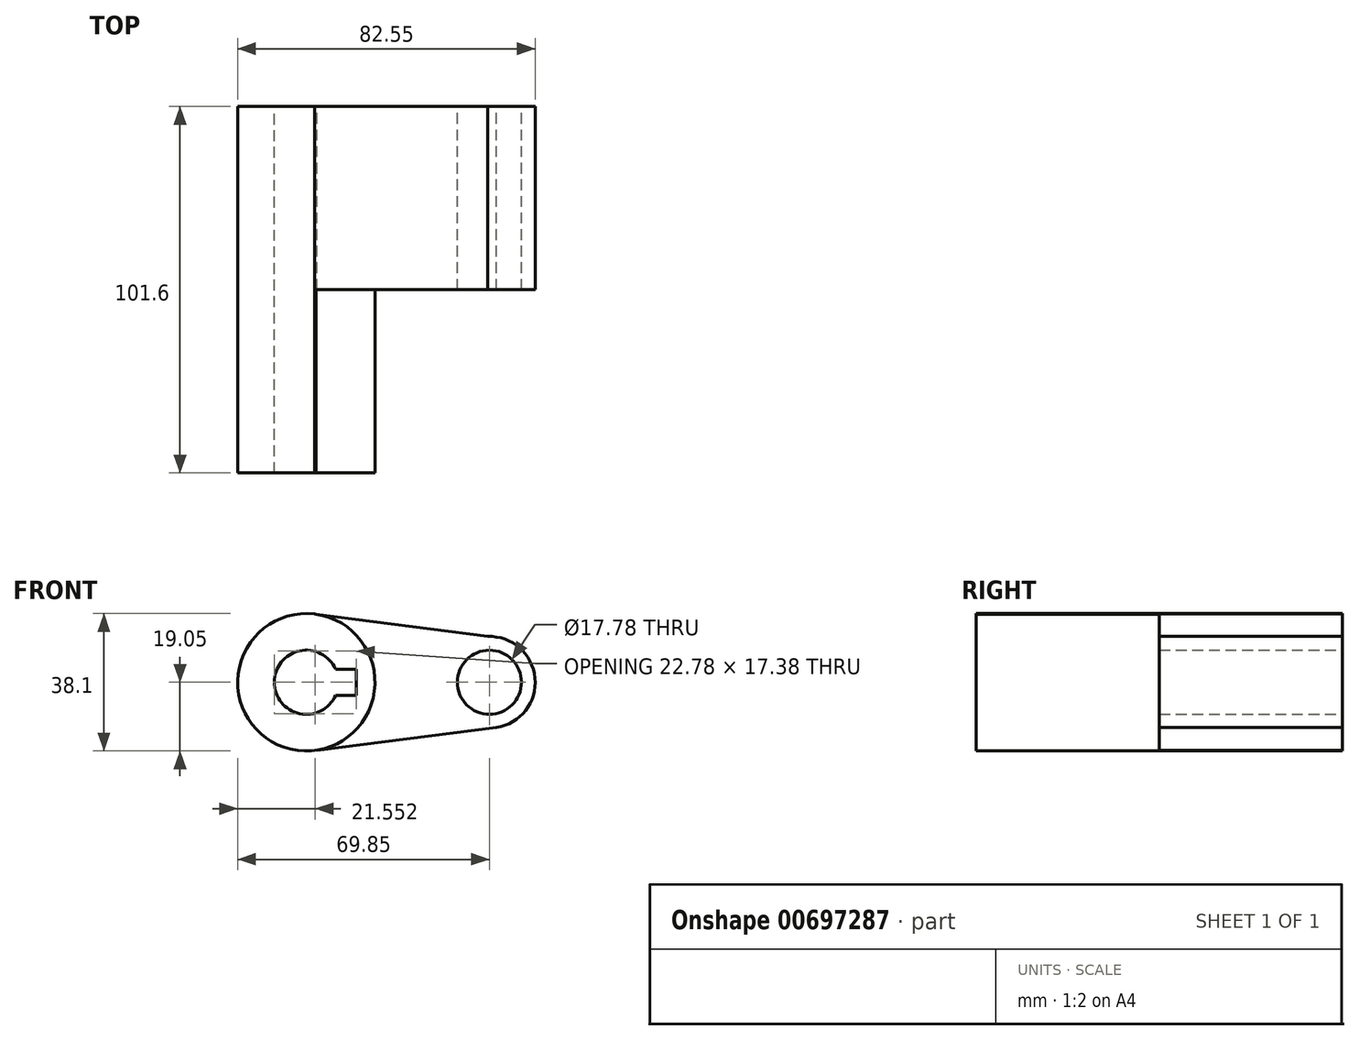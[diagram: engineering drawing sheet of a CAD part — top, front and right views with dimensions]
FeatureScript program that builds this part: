
annotation { "Feature Type Name" : "Feature", "Feature Type Description" : "" }
export const myFeature = defineFeature(function(context is Context, id is Id, definition is map)
    precondition{}
    {
        {
            var Q0;
            Q0=qCreatedBy(makeId("Front.planeOp"),FACE);
            var sketch = newSketch(context, id + "F0", { "sketchPlane" : qUnion([Q0])});
            skCircle(sketch, "E0", {"center": v(0, 0) * mm, "radius": 19.05 * mm});
            skCircle(sketch, "E1", {"center": v(50.8, 0) * mm, "radius": 12.7 * mm});
            skLineSegment(sketch, "E2", {"start": v(2.25, 18.92) * mm, "end": v(50.31, 12.7) * mm});
            skLineSegment(sketch, "E3", {"start": v(2.95, -18.82) * mm, "end": v(52.74, -12.55) * mm});
            skCircle(sketch, "E4", {"center": v(0, 0) * mm, "radius": 8.9 * mm});
            skCircle(sketch, "E5", {"center": v(50.8, 0) * mm, "radius": 8.9 * mm});
            skLineSegment(sketch, "E6.bottom", {"start": v(13.9, -3.65) * mm, "end": v(-13.9, -3.65) * mm});
            skLineSegment(sketch, "E6.top", {"start": v(13.9, 3.65) * mm, "end": v(-13.9, 3.65) * mm});
            skLineSegment(sketch, "E6.left", {"start": v(13.9, -3.65) * mm, "end": v(13.9, 3.65) * mm});
            skLineSegment(sketch, "E6.right", {"start": v(-13.9, -3.65) * mm, "end": v(-13.9, 3.65) * mm});
            skSolve(sketch);
        }
        {
            var Q0;
            {var subQ4=sQuery(id+"F0.wireOp",EDGE,"E6.left");Q0=makeQuery(id+"F0.imprint","IMPRINT",FACE,{"disambiguationData":[TD([[makeQuery(id+"F0.imprint","IMPRINT",EDGE,{"derivedFrom":subQ4}),-1.0]])]});}
            var Q1;
            {var subQ5=sQuery(id+"F0.wireOp",EDGE,"E6.right");Q1=makeQuery(id+"F0.imprint","IMPRINT",FACE,{"disambiguationData":[TD([[makeQuery(id+"F0.imprint","IMPRINT",EDGE,{"derivedFrom":subQ5}),-1.0]])]});}
            var Q2;
            {var subQ0=sQuery(id+"F0.wireOp",EDGE,"E3");var subQ1=sQuery(id+"F0.wireOp",EDGE,"E0");var subQ2=makeQuery(id+"F0.imprint","INTERSECT",VERTEX,{"derivedFrom":[subQ1,subQ0]});Q2=makeQuery(id+"F0.imprint","IMPRINT",FACE,{"disambiguationData":[TD([[makeQuery(id+"F0.imprint","IMPRINT",EDGE,{"disambiguationData":[TD([[subQ2,-1.0]])],"derivedFrom":subQ1}),-1.0]])]});}
            var Q3;
            Q3=makeQuery(id+"F0.imprint","IMPRINT",FACE,{"disambiguationData":[TD([[makeQuery(id+"F0.imprint","IMPRINT",EDGE,{"derivedFrom":sQuery(id+"F0.wireOp",EDGE,"E5")}),-1.0]])]});
            extrude(context, id + "F1", {"entities" : qUnion([Q0, Q1, Q2, Q3]), "depth" : 50.8 * mm, "offsetDistance" : 25.4 * mm});
        }
        {
            var Q0;
            {var subQ4=sQuery(id+"F0.wireOp",EDGE,"E6.left");Q0=makeQuery(id+"F0.imprint","IMPRINT",FACE,{"disambiguationData":[TD([[makeQuery(id+"F0.imprint","IMPRINT",EDGE,{"derivedFrom":subQ4}),-1.0]])]});}
            var Q1;
            {var subQ5=sQuery(id+"F0.wireOp",EDGE,"E6.right");Q1=makeQuery(id+"F0.imprint","IMPRINT",FACE,{"disambiguationData":[TD([[makeQuery(id+"F0.imprint","IMPRINT",EDGE,{"derivedFrom":subQ5}),-1.0]])]});}
            extrude(context, id + "F2", {"entities" : qUnion([Q0, Q1]), "operationType" : NewBodyOperationType.ADD, "depth" : 101.6 * mm, "offsetDistance" : 25.4 * mm});
        }
    });
